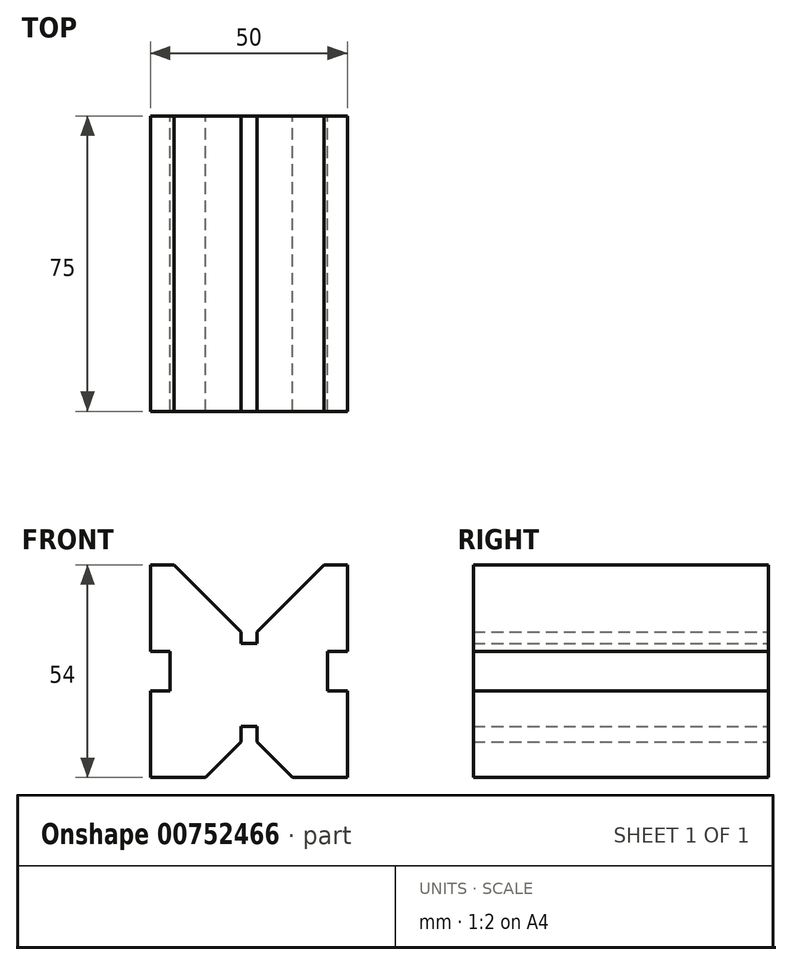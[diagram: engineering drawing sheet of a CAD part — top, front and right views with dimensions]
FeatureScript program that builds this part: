
annotation { "Feature Type Name" : "Feature", "Feature Type Description" : "" }
export const myFeature = defineFeature(function(context is Context, id is Id, definition is map)
    precondition{}
    {
        {
            var Q0;
            Q0=qCreatedBy(makeId("Front.planeOp"),FACE);
            var sketch = newSketch(context, id + "F0", { "sketchPlane" : qUnion([Q0])});
            skLineSegment(sketch, "E0", {"start": v(25, -19.01) * mm, "end": v(11, -19.01) * mm});
            skLineSegment(sketch, "E1", {"start": v(0, 37.64) * mm, "end": v(0, -28.93) * mm, "construction": true});
            skLineSegment(sketch, "E2", {"start": v(0, -6.1) * mm, "end": v(1.02, -6.1) * mm});
            skLineSegment(sketch, "E3", {"start": v(-2, -6.1) * mm, "end": v(2, -6.1) * mm});
            skLineSegment(sketch, "E4", {"start": v(-2, -6.1) * mm, "end": v(-2, -10.01) * mm});
            skLineSegment(sketch, "E5", {"start": v(2, -6.1) * mm, "end": v(2, -10.01) * mm});
            skLineSegment(sketch, "E6", {"start": v(-11, -15.11) * mm, "end": v(-11, -22.9) * mm, "construction": true});
            skLineSegment(sketch, "E7", {"start": v(11, -14.63) * mm, "end": v(11, -22.42) * mm, "construction": true});
            skLineSegment(sketch, "E8", {"start": v(2, -10.01) * mm, "end": v(11, -19.01) * mm});
            skLineSegment(sketch, "E9", {"start": v(-2, -10.01) * mm, "end": v(-11, -19.01) * mm});
            skPoint(sketch, "E9.endSnap0", {"position": v(-11, -19) * mm});
            skLineSegment(sketch, "E10.trimOffspring", {"start": v(-11, -19.01) * mm, "end": v(-25, -19.01) * mm});
            skLineSegment(sketch, "E11", {"start": v(-25, -19.01) * mm, "end": v(-25, 2.99) * mm});
            skLineSegment(sketch, "E12", {"start": v(-25, 2.99) * mm, "end": v(-20, 2.99) * mm});
            skLineSegment(sketch, "E13", {"start": v(-20, 2.99) * mm, "end": v(-20, 12.99) * mm});
            skLineSegment(sketch, "E14", {"start": v(-20, 12.99) * mm, "end": v(-25, 12.99) * mm});
            skLineSegment(sketch, "E15", {"start": v(-25, 12.99) * mm, "end": v(-25, 34.99) * mm});
            skLineSegment(sketch, "E16", {"start": v(-25, 34.99) * mm, "end": v(-19, 34.99) * mm});
            skLineSegment(sketch, "E17.MirrorCS", {"start": v(25, -19.01) * mm, "end": v(25, 2.99) * mm});
            skLineSegment(sketch, "E18.MirrorCS", {"start": v(25, 2.99) * mm, "end": v(20, 2.99) * mm});
            skLineSegment(sketch, "E19.MirrorCS", {"start": v(20, 2.99) * mm, "end": v(20, 12.99) * mm});
            skLineSegment(sketch, "E20.MirrorCS", {"start": v(20, 12.99) * mm, "end": v(25, 12.99) * mm});
            skLineSegment(sketch, "E21.MirrorCS", {"start": v(25, 12.99) * mm, "end": v(25, 34.99) * mm});
            skLineSegment(sketch, "E22.MirrorCS", {"start": v(25, 34.99) * mm, "end": v(19, 34.99) * mm});
            skLineSegment(sketch, "E23", {"start": v(-19, 34.99) * mm, "end": v(19, 34.99) * mm, "construction": true});
            skLineSegment(sketch, "E24", {"start": v(2, 14.99) * mm, "end": v(-2, 14.99) * mm});
            skLineSegment(sketch, "E25", {"start": v(-19, 34.99) * mm, "end": v(-2, 17.99) * mm});
            skLineSegment(sketch, "E26", {"start": v(-2, 14.99) * mm, "end": v(-2, 17.99) * mm});
            skLineSegment(sketch, "E27.MirrorCS", {"start": v(19, 34.99) * mm, "end": v(2, 17.99) * mm});
            skLineSegment(sketch, "E28.MirrorCS", {"start": v(2, 14.99) * mm, "end": v(2, 17.99) * mm});
            skSolve(sketch);
        }
        {
            var Q0;
            Q0=makeQuery(id+"F0.imprint","IMPRINT",FACE,{"disambiguationData":[TD([[makeQuery(id+"F0.imprint","IMPRINT",EDGE,{"derivedFrom":sQuery(id+"F0.wireOp",EDGE,"E0")}),-1.0]])]});
            extrude(context, id + "F1", {"entities" : qUnion([Q0]), "depth" : 37.5 * mm, "offsetDistance" : 25 * mm, "hasSecondDirection" : true, "secondDirectionOppositeDirection" : true, "secondDirectionDepth" : 37.5 * mm});
        }
    });
